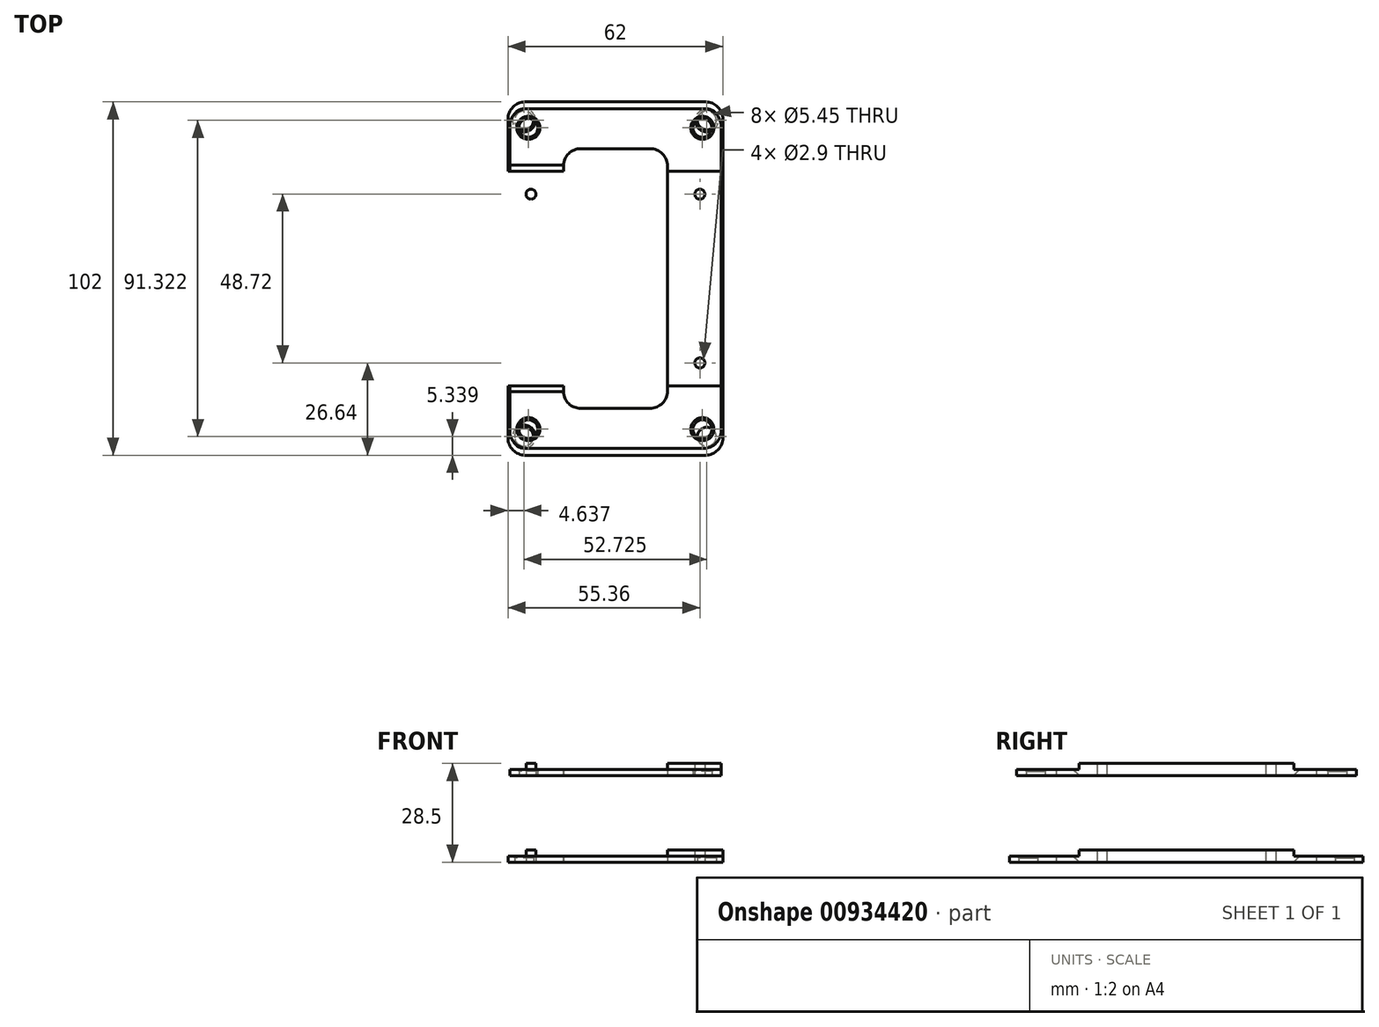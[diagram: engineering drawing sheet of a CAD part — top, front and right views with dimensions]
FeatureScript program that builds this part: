
annotation { "Feature Type Name" : "Feature", "Feature Type Description" : "" }
export const myFeature = defineFeature(function(context is Context, id is Id, definition is map)
    precondition{}
    {
        {
            var Q0;
            Q0=qCreatedBy(makeId("Top.planeOp"),FACE);
            cPlane(context, id + "F0", {"entities" : qUnion([Q0]), "cplaneType" : CPlaneType.OFFSET, "offset" : 25 * mm, "width" : 150 * mm, "height" : 150 * mm});
        }
        {
            var Q0;
            Q0=qCreatedBy(makeId("Top.planeOp"),FACE);
            var sketch = newSketch(context, id + "F1", { "sketchPlane" : qUnion([Q0])});
            skPoint(sketch, "E0.middle", {"position": v(0, 0) * mm});
            skCircle(sketch, "E1", {"center": v(24.36, 24.36) * mm, "radius": 1.45 * mm});
            skCircle(sketch, "E2.MirrorC", {"center": v(-24.36, 24.36) * mm, "radius": 1.45 * mm});
            skCircle(sketch, "E3.MirrorC", {"center": v(-24.36, -24.36) * mm, "radius": 1.45 * mm});
            skCircle(sketch, "E4.MirrorC", {"center": v(24.36, -24.36) * mm, "radius": 1.45 * mm});
            skLineSegment(sketch, "E5", {"start": v(0, 50) * mm, "end": v(0, -50) * mm, "construction": true});
            skLineSegment(sketch, "E6", {"start": v(-33, 0) * mm, "end": v(33, 0) * mm, "construction": true});
            skCircle(sketch, "E7", {"center": v(0, 0) * mm, "radius": 1.5 * mm, "construction": true});
            skCircle(sketch, "E8", {"center": v(26.36, 45.66) * mm, "radius": 2.73 * mm});
            skCircle(sketch, "E9", {"center": v(-26.36, -45.66) * mm, "radius": 2.73 * mm});
            skLineSegment(sketch, "E10", {"start": v(-23.33, 23.33) * mm, "end": v(23.33, -23.33) * mm, "construction": true});
            skLineSegment(sketch, "E11", {"start": v(23.33, 23.33) * mm, "end": v(-23.33, -23.33) * mm, "construction": true});
            skLineSegment(sketch, "E12", {"start": v(-25, 43.3) * mm, "end": v(25, -43.3) * mm, "construction": true});
            skLineSegment(sketch, "E13.MirrorCS", {"start": v(25, 43.3) * mm, "end": v(-25, -43.3) * mm, "construction": true});
            skCircle(sketch, "E14", {"center": v(0, 0) * mm, "radius": 2.5 * mm, "construction": true});
            skCircle(sketch, "E15.MirrorC", {"center": v(26.36, -45.66) * mm, "radius": 2.73 * mm});
            skCircle(sketch, "E16.MirrorC", {"center": v(-26.36, 45.66) * mm, "radius": 2.73 * mm});
            skLineSegment(sketch, "E17.bottom", {"start": v(-31, 51) * mm, "end": v(31, 51) * mm});
            skLineSegment(sketch, "E17.top", {"start": v(-31, -51) * mm, "end": v(31, -51) * mm});
            skLineSegment(sketch, "E17.left", {"start": v(-31, 51) * mm, "end": v(-31, -51) * mm});
            skLineSegment(sketch, "E17.right", {"start": v(31, 51) * mm, "end": v(31, -51) * mm});
            skLineSegment(sketch, "E18.bottom", {"start": v(-15, 37.5) * mm, "end": v(15, 37.5) * mm});
            skLineSegment(sketch, "E18.top", {"start": v(-15, -37.5) * mm, "end": v(15, -37.5) * mm});
            skLineSegment(sketch, "E18.left", {"start": v(-15, 37.5) * mm, "end": v(-15, -37.5) * mm});
            skLineSegment(sketch, "E18.right", {"start": v(15, 37.5) * mm, "end": v(15, -37.5) * mm});
            skLineSegment(sketch, "E19.bottom", {"start": v(31, -31) * mm, "end": v(-31, -31) * mm});
            skLineSegment(sketch, "E19.top", {"start": v(31, 31) * mm, "end": v(-31, 31) * mm});
            skSolve(sketch);
        }
        {
            var Q0;
            Q0=qCreatedBy(id+"F0.planeOp",FACE);
            var sketch = newSketch(context, id + "F2", { "sketchPlane" : qUnion([Q0])});
            skPoint(sketch, "E20.middle", {"position": v(0, 0) * mm});
            skCircle(sketch, "E21", {"center": v(24.36, 24.36) * mm, "radius": 1.45 * mm});
            skCircle(sketch, "E22.MirrorC", {"center": v(-24.36, 24.36) * mm, "radius": 1.45 * mm});
            skCircle(sketch, "E23.MirrorC", {"center": v(-24.36, -24.36) * mm, "radius": 1.45 * mm});
            skCircle(sketch, "E24.MirrorC", {"center": v(24.36, -24.36) * mm, "radius": 1.45 * mm});
            skLineSegment(sketch, "E25", {"start": v(0, 50) * mm, "end": v(0, -50) * mm, "construction": true});
            skLineSegment(sketch, "E26", {"start": v(-33, 0) * mm, "end": v(33, 0) * mm, "construction": true});
            skCircle(sketch, "E27", {"center": v(0, 0) * mm, "radius": 1.5 * mm, "construction": true});
            skCircle(sketch, "E28", {"center": v(25.11, 43.5) * mm, "radius": 2.73 * mm});
            skCircle(sketch, "E29", {"center": v(-25.11, -43.5) * mm, "radius": 2.73 * mm});
            skLineSegment(sketch, "E30", {"start": v(-23.33, 23.33) * mm, "end": v(23.33, -23.33) * mm, "construction": true});
            skLineSegment(sketch, "E31", {"start": v(23.33, 23.33) * mm, "end": v(-23.33, -23.33) * mm, "construction": true});
            skLineSegment(sketch, "E32", {"start": v(-25, 43.3) * mm, "end": v(25, -43.3) * mm, "construction": true});
            skLineSegment(sketch, "E33.MirrorCS", {"start": v(25, 43.3) * mm, "end": v(-25, -43.3) * mm, "construction": true});
            skCircle(sketch, "E34", {"center": v(0, 0) * mm, "radius": 2.5 * mm, "construction": true});
            skLineSegment(sketch, "E35.bottom", {"start": v(-31, 49) * mm, "end": v(31, 49) * mm});
            skLineSegment(sketch, "E35.top", {"start": v(-31, -49) * mm, "end": v(31, -49) * mm});
            skLineSegment(sketch, "E35.left", {"start": v(-30.5, 51) * mm, "end": v(-30.5, -51) * mm});
            skLineSegment(sketch, "E35.right", {"start": v(30.5, 51) * mm, "end": v(30.5, -51) * mm});
            skLineSegment(sketch, "E36.bottom", {"start": v(-15, 37.5) * mm, "end": v(15, 37.5) * mm});
            skLineSegment(sketch, "E36.top", {"start": v(-15, -37.5) * mm, "end": v(15, -37.5) * mm});
            skLineSegment(sketch, "E36.left", {"start": v(-15, 37.5) * mm, "end": v(-15, -37.5) * mm});
            skLineSegment(sketch, "E36.right", {"start": v(15, 37.5) * mm, "end": v(15, -37.5) * mm});
            skCircle(sketch, "E37.MirrorC", {"center": v(-25.11, 43.5) * mm, "radius": 2.73 * mm});
            skCircle(sketch, "E38.MirrorC", {"center": v(25.11, -43.5) * mm, "radius": 2.73 * mm});
            skLineSegment(sketch, "E39.bottom", {"start": v(31, -31) * mm, "end": v(-31, -31) * mm});
            skLineSegment(sketch, "E39.top", {"start": v(31, 31) * mm, "end": v(-31, 31) * mm});
            skSolve(sketch);
        }
        {
            var Q0;
            Q0=makeQuery(id+"F1.imprint","IMPRINT",FACE,{"disambiguationData":[TD([[makeQuery(id+"F1.imprint","IMPRINT",EDGE,{"derivedFrom":sQuery(id+"F1.wireOp",EDGE,"E9")}),-1.0]])]});
            var Q1;
            Q1=makeQuery(id+"F2.imprint","IMPRINT",FACE,{"disambiguationData":[TD([[makeQuery(id+"F2.imprint","IMPRINT",EDGE,{"derivedFrom":sQuery(id+"F2.wireOp",EDGE,"E29")}),-1.0]])]});
            var Q2;
            Q2=makeQuery(id+"F1.imprint","IMPRINT",FACE,{"disambiguationData":[TD([[makeQuery(id+"F1.imprint","IMPRINT",EDGE,{"derivedFrom":sQuery(id+"F1.wireOp",EDGE,"E8")}),-1.0]])]});
            var Q3;
            Q3=makeQuery(id+"F2.imprint","IMPRINT",FACE,{"disambiguationData":[TD([[makeQuery(id+"F2.imprint","IMPRINT",EDGE,{"derivedFrom":sQuery(id+"F2.wireOp",EDGE,"E28")}),-1.0]])]});
            extrude(context, id + "F3", {"entities" : qUnion([Q0, Q1, Q2, Q3]), "depth" : 1.8 * mm, "offsetDistance" : 25 * mm});
        }
        {
            var Q0;
            Q0=makeQuery(id+"F1.imprint","IMPRINT",FACE,{"disambiguationData":[TD([[makeQuery(id+"F1.imprint","IMPRINT",EDGE,{"derivedFrom":sQuery(id+"F1.wireOp",EDGE,"E2.MirrorC")}),1.0]])]});
            var Q1;
            Q1=makeQuery(id+"F1.imprint","IMPRINT",FACE,{"disambiguationData":[TD([[makeQuery(id+"F1.imprint","IMPRINT",EDGE,{"derivedFrom":sQuery(id+"F1.wireOp",EDGE,"E1")}),-1.0]])]});
            var Q2;
            Q2=makeQuery(id+"F2.imprint","IMPRINT",FACE,{"disambiguationData":[TD([[makeQuery(id+"F2.imprint","IMPRINT",EDGE,{"derivedFrom":sQuery(id+"F2.wireOp",EDGE,"E21")}),-1.0]])]});
            var Q3;
            Q3=makeQuery(id+"F2.imprint","IMPRINT",FACE,{"disambiguationData":[TD([[makeQuery(id+"F2.imprint","IMPRINT",EDGE,{"derivedFrom":sQuery(id+"F2.wireOp",EDGE,"E22.MirrorC")}),1.0]])]});
            extrude(context, id + "F4", {"entities" : qUnion([Q0, Q1, Q2, Q3]), "operationType" : NewBodyOperationType.ADD, "depth" : 3.5 * mm, "offsetDistance" : 25 * mm});
        }
        {
            var Q0;
            {var subQ0=sQuery(id+"F1.wireOp",EDGE,"E19.bottom");Q0=makeQuery(id+"F3.opExtrude","CAP_EDGE",EDGE,{"disambiguationData":[OSD([subQ0]),TDD([makeQuery(id+"F1.imprint","IMPRINT",EDGE,{"disambiguationData":[TD([[makeQuery(id+"F1.imprint","INTERSECT",VERTEX,{"derivedFrom":[sQuery(id+"F1.wireOp",EDGE,"E17.left"),subQ0]}),1.0]])],"derivedFrom":subQ0})])],"isStart":false});}
            var Q1;
            {var subQ0=sQuery(id+"F1.wireOp",EDGE,"E19.bottom");Q1=makeQuery(id+"F3.opExtrude","CAP_EDGE",EDGE,{"disambiguationData":[OSD([subQ0]),TDD([makeQuery(id+"F1.imprint","IMPRINT",EDGE,{"disambiguationData":[TD([[makeQuery(id+"F1.imprint","INTERSECT",VERTEX,{"derivedFrom":[sQuery(id+"F1.wireOp",EDGE,"E17.right"),subQ0]}),-1.0]])],"derivedFrom":subQ0})])],"isStart":false});}
            var Q2;
            {var subQ0=sQuery(id+"F2.wireOp",EDGE,"E39.bottom");Q2=makeQuery(id+"F3.opExtrude","CAP_EDGE",EDGE,{"disambiguationData":[OSD([subQ0]),TDD([makeQuery(id+"F2.imprint","IMPRINT",EDGE,{"disambiguationData":[TD([[makeQuery(id+"F2.imprint","INTERSECT",VERTEX,{"derivedFrom":[sQuery(id+"F2.wireOp",EDGE,"E35.left"),subQ0]}),1.0]])],"derivedFrom":subQ0})])],"isStart":false});}
            var Q3;
            {var subQ0=sQuery(id+"F2.wireOp",EDGE,"E39.bottom");Q3=makeQuery(id+"F3.opExtrude","CAP_EDGE",EDGE,{"disambiguationData":[OSD([subQ0]),TDD([makeQuery(id+"F2.imprint","IMPRINT",EDGE,{"disambiguationData":[TD([[makeQuery(id+"F2.imprint","INTERSECT",VERTEX,{"derivedFrom":[sQuery(id+"F2.wireOp",EDGE,"E35.right"),subQ0]}),-1.0]])],"derivedFrom":subQ0})])],"isStart":false});}
            var Q4;
            {var subQ0=sQuery(id+"F2.wireOp",EDGE,"E39.top");Q4=makeQuery(id+"F3.opExtrude","CAP_EDGE",EDGE,{"disambiguationData":[OSD([subQ0]),TDD([makeQuery(id+"F2.imprint","IMPRINT",EDGE,{"disambiguationData":[TD([[makeQuery(id+"F2.imprint","INTERSECT",VERTEX,{"derivedFrom":[sQuery(id+"F2.wireOp",EDGE,"E35.left"),subQ0]}),1.0]])],"derivedFrom":subQ0})])],"isStart":false});}
            var Q5;
            {var subQ0=sQuery(id+"F2.wireOp",EDGE,"E39.top");Q5=makeQuery(id+"F3.opExtrude","CAP_EDGE",EDGE,{"disambiguationData":[OSD([subQ0]),TDD([makeQuery(id+"F2.imprint","IMPRINT",EDGE,{"disambiguationData":[TD([[makeQuery(id+"F2.imprint","INTERSECT",VERTEX,{"derivedFrom":[sQuery(id+"F2.wireOp",EDGE,"E35.right"),subQ0]}),-1.0]])],"derivedFrom":subQ0})])],"isStart":false});}
            var Q6;
            {var subQ0=sQuery(id+"F1.wireOp",EDGE,"E19.top");Q6=makeQuery(id+"F3.opExtrude","CAP_EDGE",EDGE,{"disambiguationData":[OSD([subQ0]),TDD([makeQuery(id+"F1.imprint","IMPRINT",EDGE,{"disambiguationData":[TD([[makeQuery(id+"F1.imprint","INTERSECT",VERTEX,{"derivedFrom":[sQuery(id+"F1.wireOp",EDGE,"E17.left"),subQ0]}),1.0]])],"derivedFrom":subQ0})])],"isStart":false});}
            var Q7;
            {var subQ0=sQuery(id+"F1.wireOp",EDGE,"E19.top");Q7=makeQuery(id+"F3.opExtrude","CAP_EDGE",EDGE,{"disambiguationData":[OSD([subQ0]),TDD([makeQuery(id+"F1.imprint","IMPRINT",EDGE,{"disambiguationData":[TD([[makeQuery(id+"F1.imprint","INTERSECT",VERTEX,{"derivedFrom":[sQuery(id+"F1.wireOp",EDGE,"E17.right"),subQ0]}),-1.0]])],"derivedFrom":subQ0})])],"isStart":false});}
            chamfer(context, id + "F5", {"entities" : qUnion([Q0, Q1, Q2, Q3, Q4, Q5, Q6, Q7]), "width" : 1.7 * mm, "tangentPropagation" : true});
        }
        {
            var Q0;
            Q0=makeQuery(id+"F3.opExtrude","SWEPT_EDGE",EDGE,{"disambiguationData":[OSD([sQuery(id+"F2.wireOp",EDGE,"E35.top"),sQuery(id+"F2.wireOp",EDGE,"E35.right")])]});
            var Q1;
            Q1=makeQuery(id+"F3.opExtrude","SWEPT_EDGE",EDGE,{"disambiguationData":[OSD([sQuery(id+"F2.wireOp",EDGE,"E35.top"),sQuery(id+"F2.wireOp",EDGE,"E35.left")])]});
            var Q2;
            Q2=makeQuery(id+"F3.opExtrude","SWEPT_EDGE",EDGE,{"disambiguationData":[OSD([sQuery(id+"F2.wireOp",EDGE,"E36.bottom"),sQuery(id+"F2.wireOp",EDGE,"E36.right")])]});
            var Q3;
            Q3=makeQuery(id+"F3.opExtrude","SWEPT_EDGE",EDGE,{"disambiguationData":[OSD([sQuery(id+"F2.wireOp",EDGE,"E36.bottom"),sQuery(id+"F2.wireOp",EDGE,"E36.left")])]});
            var Q4;
            Q4=makeQuery(id+"F3.opExtrude","SWEPT_EDGE",EDGE,{"disambiguationData":[OSD([sQuery(id+"F1.wireOp",EDGE,"E18.bottom"),sQuery(id+"F1.wireOp",EDGE,"E18.left")])]});
            var Q5;
            Q5=makeQuery(id+"F3.opExtrude","SWEPT_EDGE",EDGE,{"disambiguationData":[OSD([sQuery(id+"F1.wireOp",EDGE,"E18.bottom"),sQuery(id+"F1.wireOp",EDGE,"E18.right")])]});
            var Q6;
            Q6=makeQuery(id+"F3.opExtrude","SWEPT_EDGE",EDGE,{"disambiguationData":[OSD([sQuery(id+"F1.wireOp",EDGE,"E17.top"),sQuery(id+"F1.wireOp",EDGE,"E17.right")])]});
            var Q7;
            Q7=makeQuery(id+"F3.opExtrude","SWEPT_EDGE",EDGE,{"disambiguationData":[OSD([sQuery(id+"F1.wireOp",EDGE,"E17.top"),sQuery(id+"F1.wireOp",EDGE,"E17.left")])]});
            var Q8;
            Q8=makeQuery(id+"F3.opExtrude","SWEPT_EDGE",EDGE,{"disambiguationData":[OSD([sQuery(id+"F2.wireOp",EDGE,"E35.bottom"),sQuery(id+"F2.wireOp",EDGE,"E35.right")])]});
            var Q9;
            Q9=makeQuery(id+"F3.opExtrude","SWEPT_EDGE",EDGE,{"disambiguationData":[OSD([sQuery(id+"F1.wireOp",EDGE,"E17.bottom"),sQuery(id+"F1.wireOp",EDGE,"E17.right")])]});
            var Q10;
            Q10=makeQuery(id+"F3.opExtrude","SWEPT_EDGE",EDGE,{"disambiguationData":[OSD([sQuery(id+"F1.wireOp",EDGE,"E18.top"),sQuery(id+"F1.wireOp",EDGE,"E18.left")])]});
            var Q11;
            Q11=makeQuery(id+"F3.opExtrude","SWEPT_EDGE",EDGE,{"disambiguationData":[OSD([sQuery(id+"F2.wireOp",EDGE,"E36.top"),sQuery(id+"F2.wireOp",EDGE,"E36.left")])]});
            var Q12;
            Q12=makeQuery(id+"F3.opExtrude","SWEPT_EDGE",EDGE,{"disambiguationData":[OSD([sQuery(id+"F2.wireOp",EDGE,"E36.top"),sQuery(id+"F2.wireOp",EDGE,"E36.right")])]});
            var Q13;
            Q13=makeQuery(id+"F3.opExtrude","SWEPT_EDGE",EDGE,{"disambiguationData":[OSD([sQuery(id+"F1.wireOp",EDGE,"E18.top"),sQuery(id+"F1.wireOp",EDGE,"E18.right")])]});
            var Q14;
            Q14=makeQuery(id+"F3.opExtrude","SWEPT_EDGE",EDGE,{"disambiguationData":[OSD([sQuery(id+"F2.wireOp",EDGE,"E35.bottom"),sQuery(id+"F2.wireOp",EDGE,"E35.left")])]});
            var Q15;
            Q15=makeQuery(id+"F3.opExtrude","SWEPT_EDGE",EDGE,{"disambiguationData":[OSD([sQuery(id+"F1.wireOp",EDGE,"E17.bottom"),sQuery(id+"F1.wireOp",EDGE,"E17.left")])]});
            fillet(context, id + "F6", {"entities" : qUnion([Q0, Q1, Q2, Q3, Q4, Q5, Q6, Q7, Q8, Q9, Q10, Q11, Q12, Q13, Q14, Q15]), "radius" : 5 * mm, "tangentPropagation" : true, "allowEdgeOverflow" : false});
        }
        {
            var Q0;
            Q0=makeQuery(id+"F3.opExtrude","CAP_EDGE",EDGE,{"disambiguationData":[OSD([sQuery(id+"F1.wireOp",EDGE,"E8")])],"isStart":false});
            var Q1;
            Q1=makeQuery(id+"F3.opExtrude","CAP_EDGE",EDGE,{"disambiguationData":[OSD([sQuery(id+"F1.wireOp",EDGE,"E16.MirrorC")])],"isStart":false});
            var Q2;
            Q2=makeQuery(id+"F3.opExtrude","CAP_EDGE",EDGE,{"disambiguationData":[OSD([sQuery(id+"F2.wireOp",EDGE,"E37.MirrorC")])],"isStart":false});
            var Q3;
            Q3=makeQuery(id+"F3.opExtrude","CAP_EDGE",EDGE,{"disambiguationData":[OSD([sQuery(id+"F2.wireOp",EDGE,"E28")])],"isStart":false});
            var Q4;
            Q4=makeQuery(id+"F3.opExtrude","CAP_EDGE",EDGE,{"disambiguationData":[OSD([sQuery(id+"F2.wireOp",EDGE,"E38.MirrorC")])],"isStart":false});
            var Q5;
            Q5=makeQuery(id+"F3.opExtrude","CAP_EDGE",EDGE,{"disambiguationData":[OSD([sQuery(id+"F2.wireOp",EDGE,"E29")])],"isStart":false});
            var Q6;
            Q6=makeQuery(id+"F3.opExtrude","CAP_EDGE",EDGE,{"disambiguationData":[OSD([sQuery(id+"F1.wireOp",EDGE,"E9")])],"isStart":false});
            chamfer(context, id + "F7", {"entities" : qUnion([Q0, Q1, Q2, Q3, Q4, Q5, Q6]), "width" : 0.6 * mm, "tangentPropagation" : true});
        }
    });
